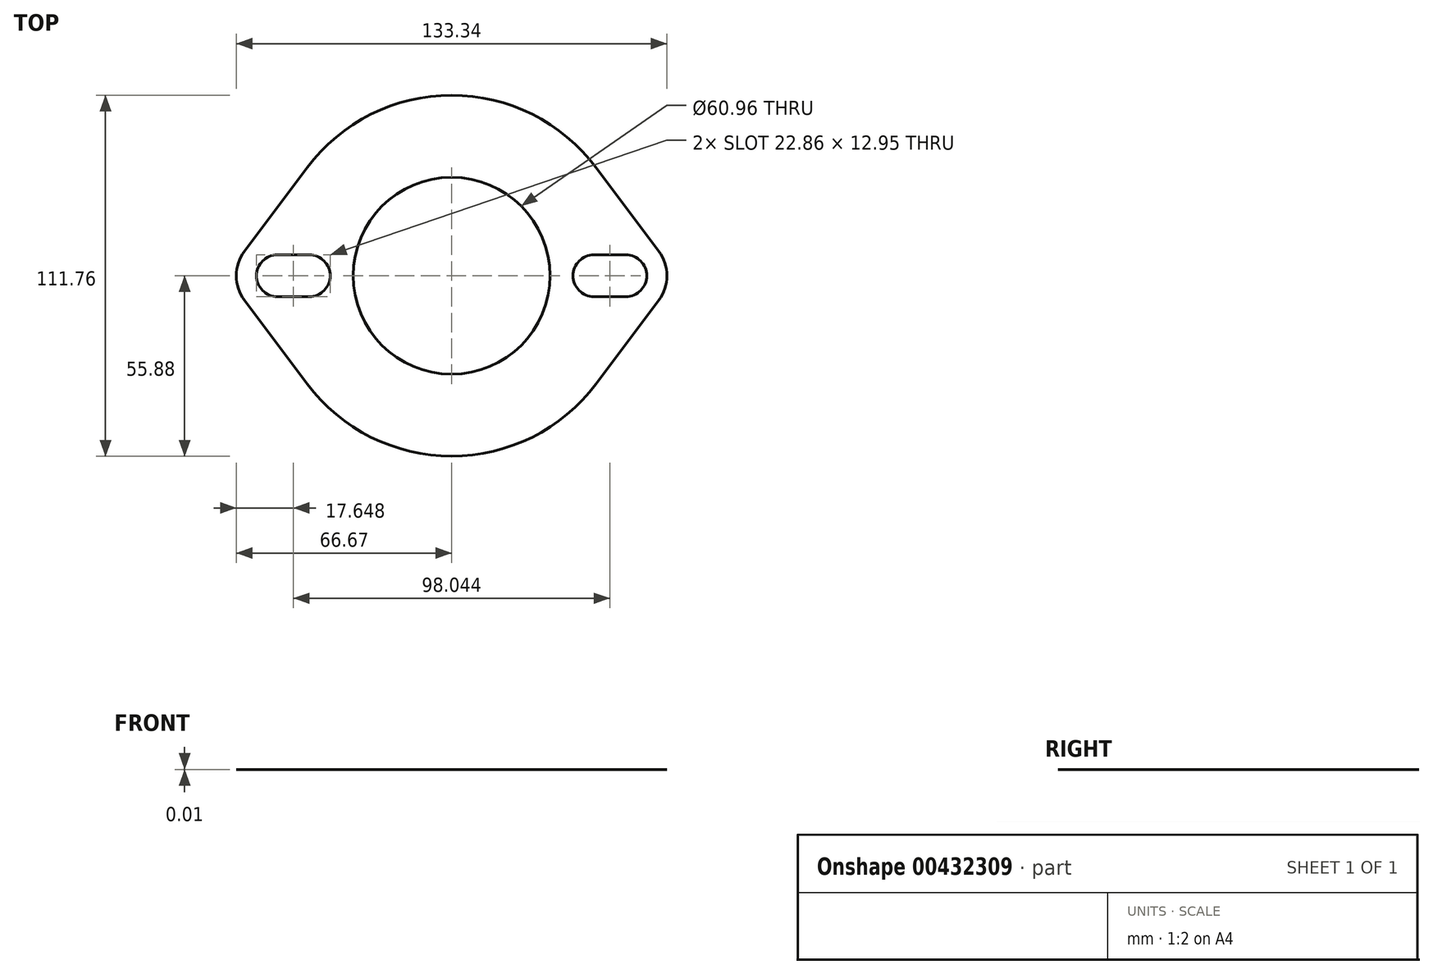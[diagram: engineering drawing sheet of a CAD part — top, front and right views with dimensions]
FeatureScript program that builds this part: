
annotation { "Feature Type Name" : "Feature", "Feature Type Description" : "" }
export const myFeature = defineFeature(function(context is Context, id is Id, definition is map)
    precondition{}
    {
        {
            var Q0;
            Q0=qCreatedBy(makeId("Top.planeOp"),FACE);
            var sketch = newSketch(context, id + "F0", { "sketchPlane" : qUnion([Q0])});
            skCircle(sketch, "E0", {"center": v(0, 0) * mm, "radius": 30.48 * mm});
            skArc(sketch, "E1", {"start": v(-44.7, -33.53) * mm, "mid": v(0, -55.88) * mm, "end": v(44.7, -33.53) * mm});
            skArc(sketch, "E2", {"start": v(-53.98, 6.48) * mm, "mid": v(-60.45, 0) * mm, "end": v(-53.98, -6.48) * mm});
            skArc(sketch, "E3", {"start": v(-44.07, -6.48) * mm, "mid": v(-37.6, 0) * mm, "end": v(-44.07, 6.48) * mm});
            skArc(sketch, "E4", {"start": v(44.07, 6.48) * mm, "mid": v(37.6, 0) * mm, "end": v(44.07, -6.48) * mm});
            skArc(sketch, "E5", {"start": v(53.98, -6.48) * mm, "mid": v(60.45, 0) * mm, "end": v(53.98, 6.48) * mm});
            skLineSegment(sketch, "E6", {"start": v(-53.98, 6.48) * mm, "end": v(-44.07, 6.48) * mm});
            skLineSegment(sketch, "E7", {"start": v(-44.07, -6.48) * mm, "end": v(-53.98, -6.48) * mm});
            skLineSegment(sketch, "E8", {"start": v(44.07, 6.48) * mm, "end": v(53.98, 6.48) * mm});
            skLineSegment(sketch, "E9", {"start": v(53.98, -6.48) * mm, "end": v(44.07, -6.48) * mm});
            skLineSegment(sketch, "E10", {"start": v(-64.14, 7.62) * mm, "end": v(-44.7, 33.53) * mm});
            skLineSegment(sketch, "E11", {"start": v(44.7, 33.53) * mm, "end": v(64.14, 7.62) * mm});
            skLineSegment(sketch, "E12", {"start": v(64.14, -7.62) * mm, "end": v(44.7, -33.53) * mm});
            skLineSegment(sketch, "E13", {"start": v(-44.7, -33.53) * mm, "end": v(-64.14, -7.62) * mm});
            skArc(sketch, "E14.trimOffspring", {"start": v(44.7, 33.53) * mm, "mid": v(0, 55.88) * mm, "end": v(-44.7, 33.53) * mm});
            skLineSegment(sketch, "E15", {"start": v(-60.45, 0) * mm, "end": v(-53.98, 0) * mm, "construction": true});
            skLineSegment(sketch, "E16", {"start": v(-44.07, 0) * mm, "end": v(0, 0) * mm, "construction": true});
            skLineSegment(sketch, "E17", {"start": v(0, 0) * mm, "end": v(44.07, 0) * mm, "construction": true});
            skLineSegment(sketch, "E18", {"start": v(53.98, 0) * mm, "end": v(60.45, 0) * mm, "construction": true});
            skPoint(sketch, "E19", {"position": v(-60.45, 0) * mm});
            skPoint(sketch, "E20", {"position": v(-37.6, 0) * mm});
            skPoint(sketch, "E21", {"position": v(37.6, 0) * mm});
            skPoint(sketch, "E22", {"position": v(60.45, 0) * mm});
            skPoint(sketch, "E23", {"position": v(-66.68, 0) * mm});
            skPoint(sketch, "E24", {"position": v(66.67, 0) * mm});
            skArc(sketch, "E25", {"start": v(-64.13, 7.62) * mm, "mid": v(-66.68, 0) * mm, "end": v(-64.14, -7.62) * mm});
            skArc(sketch, "E26", {"start": v(64.14, -7.62) * mm, "mid": v(66.68, 0) * mm, "end": v(64.13, 7.62) * mm});
            skLineSegment(sketch, "E27", {"start": v(4.77, -30.1) * mm, "end": v(8.75, -55.2) * mm, "construction": true});
            skSolve(sketch);
        }
        {
            var Q0;
            Q0=makeQuery(id+"F0.imprint","IMPRINT",FACE,{"disambiguationData":[TD([[makeQuery(id+"F0.imprint","IMPRINT",EDGE,{"derivedFrom":sQuery(id+"F0.wireOp",EDGE,"E0")}),-1.0]])]});
            extrude(context, id + "F1", {"entities" : qUnion([Q0]), "depth" : 5 / 406.4 * mm});
        }
        {
            var Q0;
            Q0=makeQuery(id+"F1.opExtrude","SWEPT_FACE",FACE,{"disambiguationData":[OSD([sQuery(id+"F0.wireOp",EDGE,"E10")])]});
            var sketch = newSketch(context, id + "F2", { "sketchPlane" : qUnion([Q0])});
            skLineSegment(sketch, "E28", {"start": v(16.2, 7.94) * mm, "end": v(16.2, 0) * mm, "construction": true});
            skLineSegment(sketch, "E29", {"start": v(0, 3.97) * mm, "end": v(32.39, 3.97) * mm, "construction": true});
            skCircle(sketch, "E30", {"center": v(16.2, 3.97) * mm, "radius": 1.5 * mm});
            skSolve(sketch);
        }
        {
            var Q0;
            Q0=makeQuery(id+"F2.imprint","IMPRINT",FACE,{"disambiguationData":[TD([[makeQuery(id+"F2.imprint","IMPRINT",EDGE,{"derivedFrom":sQuery(id+"F2.wireOp",EDGE,"E30")}),1.0]])]});
            var Q1;
            Q1=makeQuery(id+"F1.opExtrude","SWEPT_FACE",FACE,{"disambiguationData":[OSD([sQuery(id+"F0.wireOp",EDGE,"E0")])]});
            extrude(context, id + "F3", {"entities" : qUnion([Q0]), "operationType" : NewBodyOperationType.REMOVE, "endBound" : BoundingType.UP_TO_SURFACE, "oppositeDirection" : true, "endBoundEntityFace" : qUnion([Q1]), "depth" : 25.4 * mm});
        }
    });
